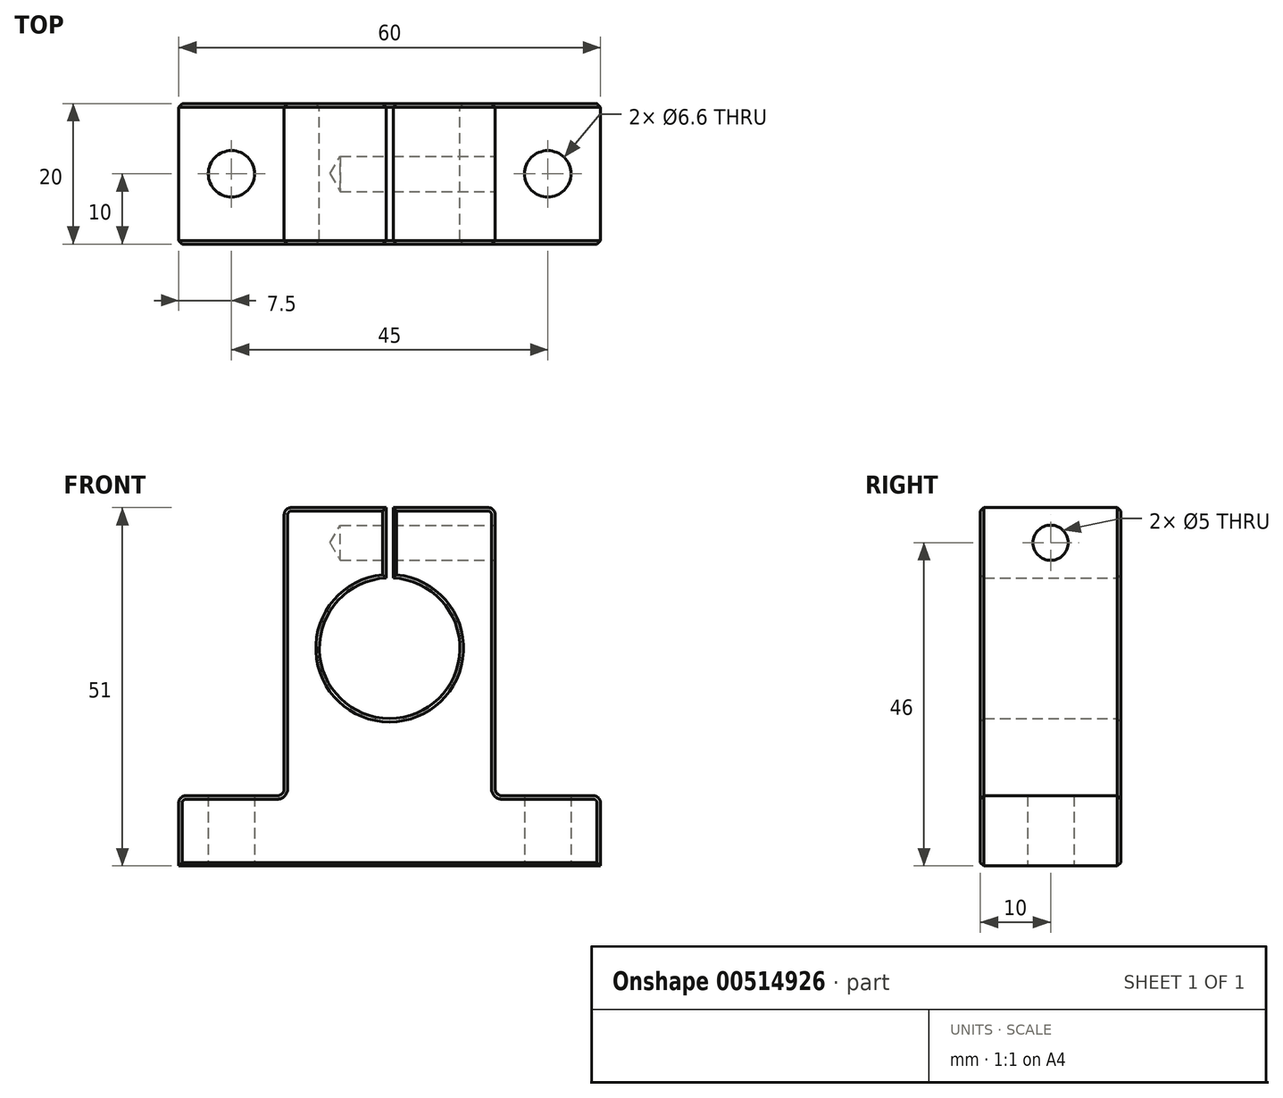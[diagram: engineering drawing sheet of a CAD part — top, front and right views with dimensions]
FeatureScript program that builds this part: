
annotation { "Feature Type Name" : "Feature", "Feature Type Description" : "" }
export const myFeature = defineFeature(function(context is Context, id is Id, definition is map)
    precondition{}
    {
        {
            var Q0;
            Q0=qCreatedBy(makeId("Front.planeOp"),FACE);
            var sketch = newSketch(context, id + "F0", { "sketchPlane" : qUnion([Q0])});
            skLineSegment(sketch, "E0", {"start": v(0.5, 51) * mm, "end": v(15, 51) * mm});
            skLineSegment(sketch, "E1", {"start": v(15, 51) * mm, "end": v(15, 10) * mm});
            skLineSegment(sketch, "E2", {"start": v(15, 10) * mm, "end": v(30, 10) * mm});
            skLineSegment(sketch, "E3", {"start": v(30, 10) * mm, "end": v(30, 0) * mm});
            skLineSegment(sketch, "E4", {"start": v(30, 0) * mm, "end": v(0, 0) * mm});
            skLineSegment(sketch, "E5", {"start": v(0, 0) * mm, "end": v(0, 21) * mm});
            skArc(sketch, "E6", {"start": v(0, 21) * mm, "mid": v(10, 30.75) * mm, "end": v(0.5, 40.99) * mm});
            skLineSegment(sketch, "E7", {"start": v(0.5, 51) * mm, "end": v(0.5, 40.99) * mm});
            skSolve(sketch);
        }
        {
            var Q0;
            Q0=makeQuery(id+"F0.imprint","IMPRINT",FACE,{"disambiguationData":[TD([[makeQuery(id+"F0.imprint","IMPRINT",EDGE,{"derivedFrom":sQuery(id+"F0.wireOp",EDGE,"E0")}),-1.0]])]});
            extrude(context, id + "F1", {"entities" : qUnion([Q0]), "endBound" : BoundingType.SYMMETRIC, "depth" : 20 * mm, "offsetDistance" : 25 * mm});
        }
        {
            var Q0;
            Q0=makeQuery(id+"F1.opExtrude","SWEPT_FACE",FACE,{"disambiguationData":[OSD([sQuery(id+"F0.wireOp",EDGE,"E4")])]});
            var sketch = newSketch(context, id + "F2", { "sketchPlane" : qUnion([Q0])});
            skPoint(sketch, "E8", {"position": v(22.5, 0) * mm});
            skSolve(sketch);
        }
        {
            var Q0;
            Q0=sQuery(id+"F2.wireOp",VERTEX,"E8");
            var Q1;
            Q1=makeQuery(id+"F1.opExtrude","SWEPT_BODY",BODY,{"disambiguationData":[OSD([sQuery(id+"F0.wireOp",EDGE,"E0"),sQuery(id+"F0.wireOp",EDGE,"E1"),sQuery(id+"F0.wireOp",EDGE,"E2"),sQuery(id+"F0.wireOp",EDGE,"E3"),sQuery(id+"F0.wireOp",EDGE,"E4"),sQuery(id+"F0.wireOp",EDGE,"E5"),sQuery(id+"F0.wireOp",EDGE,"E6"),sQuery(id+"F0.wireOp",EDGE,"E7")])]});
            hole(context, id + "F3", {"style" : HoleStyle.SIMPLE, "endStyle" : HoleEndStyle.THROUGH, "standardTappedOrClearance" : lookupTablePath({ "standard" : "ISO", "fit" : "Normal", "size" : "M6", "type" : "Clearance" }), "standardBlindInLast" : lookupTablePath({ "fit" : "Standard", "standard" : "ISO", "size" : "M6", "type" : "Clearance" }), "holeDiameter" : 6.6 * mm, "isTappedThrough" : true, "tappedDepth" : 12 * mm, "tapClearance" : 3, "locations" : qUnion([Q0]), "scope" : qUnion([Q1])});
        }
        {
            var Q0;
            Q0=makeQuery(id+"F1.opExtrude","SWEPT_BODY",BODY,{"disambiguationData":[OSD([sQuery(id+"F0.wireOp",EDGE,"E0"),sQuery(id+"F0.wireOp",EDGE,"E1"),sQuery(id+"F0.wireOp",EDGE,"E2"),sQuery(id+"F0.wireOp",EDGE,"E3"),sQuery(id+"F0.wireOp",EDGE,"E4"),sQuery(id+"F0.wireOp",EDGE,"E5"),sQuery(id+"F0.wireOp",EDGE,"E6"),sQuery(id+"F0.wireOp",EDGE,"E7")])]});
            var Q1;
            Q1=qCreatedBy(makeId("Right.planeOp"),FACE);
            mirror(context, id + "F4", {"operationType" : NewBodyOperationType.ADD, "entities" : qUnion([Q0]), "mirrorPlane" : qUnion([Q1])});
        }
        {
            var Q0;
            Q0=makeQuery(id+"F1.opExtrude","SWEPT_FACE",FACE,{"disambiguationData":[OSD([sQuery(id+"F0.wireOp",EDGE,"E1")])]});
            var sketch = newSketch(context, id + "F5", { "sketchPlane" : qUnion([Q0])});
            skPoint(sketch, "E9", {"position": v(0, 46) * mm});
            skSolve(sketch);
        }
        {
            var Q0;
            Q0=sQuery(id+"F5.wireOp",VERTEX,"E9");
            var Q1;
            Q1=makeQuery(id+"F1.opExtrude","SWEPT_BODY",BODY,{"disambiguationData":[OSD([sQuery(id+"F0.wireOp",EDGE,"E0"),sQuery(id+"F0.wireOp",EDGE,"E1"),sQuery(id+"F0.wireOp",EDGE,"E2"),sQuery(id+"F0.wireOp",EDGE,"E3"),sQuery(id+"F0.wireOp",EDGE,"E4"),sQuery(id+"F0.wireOp",EDGE,"E5"),sQuery(id+"F0.wireOp",EDGE,"E6"),sQuery(id+"F0.wireOp",EDGE,"E7")])]});
            hole(context, id + "F6", {"style" : HoleStyle.SIMPLE, "endStyle" : HoleEndStyle.BLIND, "holeDiameter" : 5 * mm, "holeDepth" : 22 * mm, "isTappedThrough" : true, "tappedDepth" : 12 * mm, "tapClearance" : 3, "locations" : qUnion([Q0]), "scope" : qUnion([Q1])});
        }
        {
            var Q0;
            Q0=makeQuery(id+"F1.opExtrude","SWEPT_EDGE",EDGE,{"disambiguationData":[OSD([sQuery(id+"F0.wireOp",EDGE,"E1"),sQuery(id+"F0.wireOp",EDGE,"E2")])]});
            var Q1;
            Q1=makeQuery(id+"F4.opPattern","COPY",EDGE,{"derivedFrom":makeQuery(id+"F1.opExtrude","SWEPT_EDGE",EDGE,{"disambiguationData":[OSD([sQuery(id+"F0.wireOp",EDGE,"E1"),sQuery(id+"F0.wireOp",EDGE,"E2")])]}),"instanceName":"1"});
            var Q2;
            Q2=makeQuery(id+"F4.opPattern","COPY",EDGE,{"derivedFrom":makeQuery(id+"F1.opExtrude","SWEPT_EDGE",EDGE,{"disambiguationData":[OSD([sQuery(id+"F0.wireOp",EDGE,"E2"),sQuery(id+"F0.wireOp",EDGE,"E3")])]}),"instanceName":"1"});
            var Q3;
            Q3=makeQuery(id+"F1.opExtrude","SWEPT_EDGE",EDGE,{"disambiguationData":[OSD([sQuery(id+"F0.wireOp",EDGE,"E2"),sQuery(id+"F0.wireOp",EDGE,"E3")])]});
            var Q4;
            Q4=makeQuery(id+"F1.opExtrude","SWEPT_EDGE",EDGE,{"disambiguationData":[OSD([sQuery(id+"F0.wireOp",EDGE,"E0"),sQuery(id+"F0.wireOp",EDGE,"E1")])]});
            var Q5;
            Q5=makeQuery(id+"F4.opPattern","COPY",EDGE,{"derivedFrom":makeQuery(id+"F1.opExtrude","SWEPT_EDGE",EDGE,{"disambiguationData":[OSD([sQuery(id+"F0.wireOp",EDGE,"E0"),sQuery(id+"F0.wireOp",EDGE,"E1")])]}),"instanceName":"1"});
            fillet(context, id + "F7", {"entities" : qUnion([Q0, Q1, Q2, Q3, Q4, Q5]), "radius" : 1 * mm, "tangentPropagation" : true, "allowEdgeOverflow" : false});
        }
        {
            var Q0;
            Q0=makeQuery(id+"F4.opPattern","COPY",EDGE,{"derivedFrom":makeQuery(id+"F1.opExtrude","CAP_EDGE",EDGE,{"disambiguationData":[OSD([sQuery(id+"F0.wireOp",EDGE,"E3")])],"isStart":false}),"instanceName":"1"});
            var Q1;
            {var subQ0=sQuery(id+"F0.wireOp",EDGE,"E3");var subQ1=sQuery(id+"F0.wireOp",EDGE,"E2");var subQ2=makeQuery(id+"F1.opExtrude","CAP_FACE",FACE,{"disambiguationData":[OSD([sQuery(id+"F0.wireOp",EDGE,"E0"),sQuery(id+"F0.wireOp",EDGE,"E1"),subQ1,subQ0,sQuery(id+"F0.wireOp",EDGE,"E4"),sQuery(id+"F0.wireOp",EDGE,"E5"),sQuery(id+"F0.wireOp",EDGE,"E6"),sQuery(id+"F0.wireOp",EDGE,"E7")])],"isStart":false});Q1=makeQuery(id+"F7.opFillet","BLEND_EDGE",EDGE,{"blendedFrom":[makeQuery(id+"F4.opPattern","COPY",EDGE,{"derivedFrom":makeQuery(id+"F1.opExtrude","SWEPT_EDGE",EDGE,{"disambiguationData":[OSD([subQ1,subQ0])]}),"instanceName":"1"}),makeQuery(id+"F4.boolean.opBoolean","MERGE",FACE,{"derivedFrom":[subQ2,makeQuery(id+"F4.opPattern","COPY",FACE,{"derivedFrom":subQ2,"instanceName":"1"})]})],"blendedInto":[makeQuery(id+"F4.boolean.opBoolean","MERGE",FACE,{"derivedFrom":[subQ2,makeQuery(id+"F4.opPattern","COPY",FACE,{"derivedFrom":subQ2,"instanceName":"1"})]})]});}
            var Q2;
            Q2=makeQuery(id+"F4.opPattern","COPY",EDGE,{"derivedFrom":makeQuery(id+"F1.opExtrude","CAP_EDGE",EDGE,{"disambiguationData":[OSD([sQuery(id+"F0.wireOp",EDGE,"E2")])],"isStart":false}),"instanceName":"1"});
            var Q3;
            {var subQ0=sQuery(id+"F0.wireOp",EDGE,"E2");var subQ1=sQuery(id+"F0.wireOp",EDGE,"E1");var subQ2=makeQuery(id+"F1.opExtrude","CAP_FACE",FACE,{"disambiguationData":[OSD([sQuery(id+"F0.wireOp",EDGE,"E0"),subQ1,subQ0,sQuery(id+"F0.wireOp",EDGE,"E3"),sQuery(id+"F0.wireOp",EDGE,"E4"),sQuery(id+"F0.wireOp",EDGE,"E5"),sQuery(id+"F0.wireOp",EDGE,"E6"),sQuery(id+"F0.wireOp",EDGE,"E7")])],"isStart":false});Q3=makeQuery(id+"F7.opFillet","BLEND_EDGE",EDGE,{"blendedFrom":[makeQuery(id+"F4.opPattern","COPY",EDGE,{"derivedFrom":makeQuery(id+"F1.opExtrude","SWEPT_EDGE",EDGE,{"disambiguationData":[OSD([subQ1,subQ0])]}),"instanceName":"1"}),makeQuery(id+"F4.boolean.opBoolean","MERGE",FACE,{"derivedFrom":[subQ2,makeQuery(id+"F4.opPattern","COPY",FACE,{"derivedFrom":subQ2,"instanceName":"1"})]})],"blendedInto":[makeQuery(id+"F4.boolean.opBoolean","MERGE",FACE,{"derivedFrom":[subQ2,makeQuery(id+"F4.opPattern","COPY",FACE,{"derivedFrom":subQ2,"instanceName":"1"})]})]});}
            var Q4;
            Q4=makeQuery(id+"F4.opPattern","COPY",EDGE,{"derivedFrom":makeQuery(id+"F1.opExtrude","CAP_EDGE",EDGE,{"disambiguationData":[OSD([sQuery(id+"F0.wireOp",EDGE,"E1")])],"isStart":false}),"instanceName":"1"});
            var Q5;
            {var subQ0=makeQuery(id+"F1.opExtrude","CAP_FACE",FACE,{"disambiguationData":[OSD([sQuery(id+"F0.wireOp",EDGE,"E0"),sQuery(id+"F0.wireOp",EDGE,"E1"),sQuery(id+"F0.wireOp",EDGE,"E2"),sQuery(id+"F0.wireOp",EDGE,"E3"),sQuery(id+"F0.wireOp",EDGE,"E4"),sQuery(id+"F0.wireOp",EDGE,"E5"),sQuery(id+"F0.wireOp",EDGE,"E6"),sQuery(id+"F0.wireOp",EDGE,"E7")])],"isStart":false});Q5=makeQuery(id+"F4.boolean.opBoolean","MERGE",FACE,{"derivedFrom":[subQ0,makeQuery(id+"F4.opPattern","COPY",FACE,{"derivedFrom":subQ0,"instanceName":"1"})]});}
            var Q6;
            {var subQ0=makeQuery(id+"F1.opExtrude","CAP_FACE",FACE,{"disambiguationData":[OSD([sQuery(id+"F0.wireOp",EDGE,"E0"),sQuery(id+"F0.wireOp",EDGE,"E1"),sQuery(id+"F0.wireOp",EDGE,"E2"),sQuery(id+"F0.wireOp",EDGE,"E3"),sQuery(id+"F0.wireOp",EDGE,"E4"),sQuery(id+"F0.wireOp",EDGE,"E5"),sQuery(id+"F0.wireOp",EDGE,"E6"),sQuery(id+"F0.wireOp",EDGE,"E7")])],"isStart":true});Q6=makeQuery(id+"F4.boolean.opBoolean","MERGE",FACE,{"derivedFrom":[subQ0,makeQuery(id+"F4.opPattern","COPY",FACE,{"derivedFrom":subQ0,"instanceName":"1"})]});}
            chamfer(context, id + "F8", {"entities" : qUnion([Q0, Q1, Q2, Q3, Q4, Q5, Q6]), "width" : 0.5 * mm, "tangentPropagation" : true});
        }
    });
